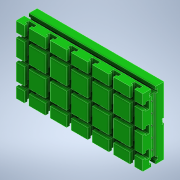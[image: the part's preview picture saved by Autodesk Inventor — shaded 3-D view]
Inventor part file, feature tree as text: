
AUTODESK INVENTOR PART (.ipt)
format: ipt  version: 2021 (Build 250183000, 183)  size: 1,183,232 bytes
history: native  units: mm
features: sketch x9, other x5, pattern_linear x5, mirror x3, hole x3, extrude x1
ambient origin geometry x8: Origin, YZ Plane, XZ Plane, XY Plane, X Axis, Y Axis, Z Axis, Center Point
bodies: Solid1 (feature_tree)
feature tree (26):
  extrude  "Extrusion1"  Depth=384.0mm
  other  "iFeature2:1"
  other  "iFeature2:2"
  pattern_linear  "Rectangular Pattern1"  Spacing1=7.0mm  [1 undecoded]
  pattern_linear  "Rectangular Pattern2"  Spacing1=38.0mm  [1 undecoded]
  other  "iFeature2:3"
  mirror  "Mirror1"
  other  "iFeature4:1"
  other  "iFeature4:2"
  mirror  "Mirror2"
  hole  "Hole1"  [1 undecoded]
  pattern_linear  "Rectangular Pattern3"  Spacing1=64.0mm  [1 undecoded]
  mirror  "Mirror3"
  hole  "Hole2"  [1 undecoded]
  pattern_linear  "Rectangular Pattern4"  Spacing1=64.0mm  [1 undecoded]
  hole  "Hole3"  [1 undecoded]
  pattern_linear  "Rectangular Pattern5"  Spacing1=32.0mm  [1 undecoded]
  sketch  "Sketch1"  dims[d0=384.0mm d1=204.0mm]
  sketch  "Sketch7"  dims[d11=7.0mm]
  sketch  "Sketch8"  dims[d12=32.0mm]
  sketch  "Sketch9"  dims[d13=10.0mm d14=9.0mm d15=14.0mm d16=25.0mm d17=12.5mm d18=7.0mm d19=38.0mm d20=60.0mm d22=64.0mm d23=30.0mm d25=64.0mm d26=10.0mm d27=9.0mm d28=14.0mm d29=25.0mm d30=12.5mm d31=7.0mm d32=32.0mm d33=7.0mm d34=2.0mm d35=2.0mm d36=90.0deg d37=2.0mm d38=135.0deg d39=5.0mm d40=7.0mm d41=2.0mm d42=2.0mm d43=90.0deg d44=2.0mm d45=135.0deg d46=5.0mm d47=32.0mm d48=38.0mm d49=32.0mm d50=4.917mm d51=10.0mm d52=4.0mm d53=2.0mm d54=90.0deg d55=15.0mm d56=20.594885mm d57=50.0mm d59=32.0mm d60=64.0mm d61=70.0mm d62=46.0mm d63=10.0mm d64=4.0mm d65=2.0mm d66=90.0deg d67=35.0mm d68=20.594885mm d69=50.0mm d71=64.0mm d72=20.0mm d74=64.0mm d75=32.0mm d76=102.0mm d77=4.917mm d78=10.0mm d79=4.0mm d80=2.0mm d81=90.0deg d82=15.0mm d83=20.594885mm d84=70.0mm d86=64.0mm d58=0.75mm]
  sketch  "Sketch2"  dims[d2=192.0mm]
  sketch  "Sketch3"  dims[d3=102.0mm]
  sketch  "Sketch4"  dims[d4=64.0mm]
  sketch  "Sketch5"  dims[d5=0.0mm]
  sketch  "Sketch6"  dims[d6=10.0mm d7=9.0mm d8=14.0mm d9=25.0mm d10=12.5mm]
note: 8 required parameter values undecoded (feature->parameter linkage not recoverable at this tier; creation-order binding heuristic only, values carry confidence <= 0.55)
